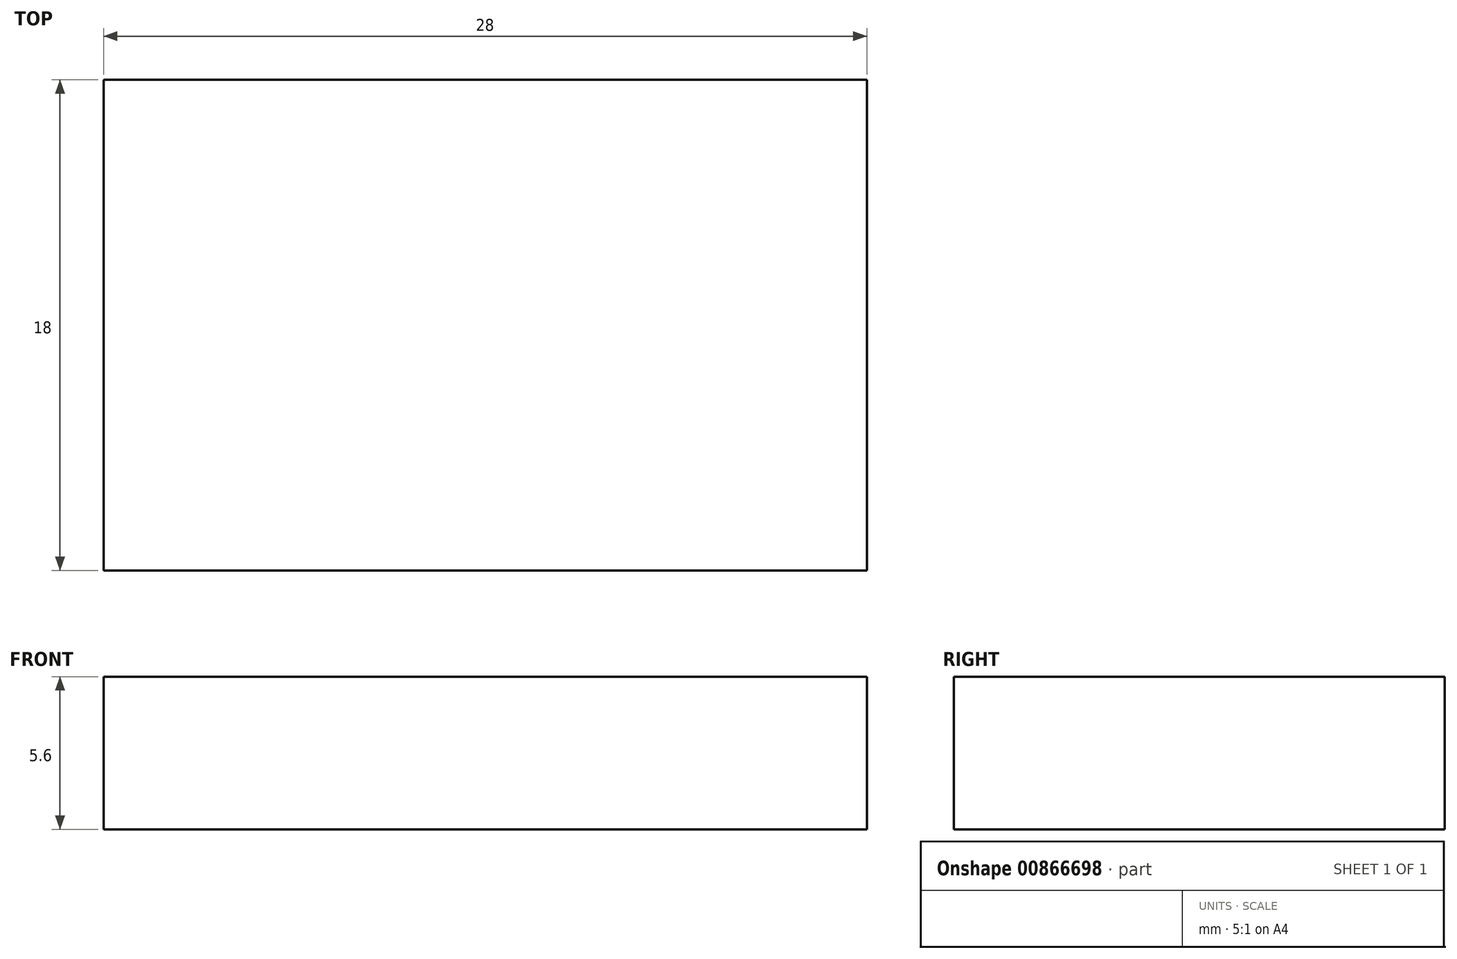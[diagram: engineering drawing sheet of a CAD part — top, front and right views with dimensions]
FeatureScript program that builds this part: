
annotation { "Feature Type Name" : "Feature", "Feature Type Description" : "" }
export const myFeature = defineFeature(function(context is Context, id is Id, definition is map)
    precondition{}
    {
        {
            var Q0;
            Q0=qCreatedBy(makeId("Top.planeOp"),FACE);
            var sketch = newSketch(context, id + "F0", { "sketchPlane" : qUnion([Q0])});
            skLineSegment(sketch, "E0.bottom", {"start": v(14, -9) * mm, "end": v(-14, -9) * mm});
            skLineSegment(sketch, "E0.top", {"start": v(14, 9) * mm, "end": v(-14, 9) * mm});
            skLineSegment(sketch, "E0.left", {"start": v(14, -9) * mm, "end": v(14, 9) * mm});
            skLineSegment(sketch, "E0.right", {"start": v(-14, -9) * mm, "end": v(-14, 9) * mm});
            skPoint(sketch, "E0.middle", {"position": v(0, 0) * mm});
            skSolve(sketch);
        }
        {
            var Q0;
            Q0=makeQuery(id+"F0.imprint","IMPRINT",FACE,{"disambiguationData":[TD([[makeQuery(id+"F0.imprint","IMPRINT",EDGE,{"derivedFrom":sQuery(id+"F0.wireOp",EDGE,"E0.bottom")}),-1.0]])]});
            extrude(context, id + "F1", {"entities" : qUnion([Q0]), "depth" : 5.6 * mm, "offsetDistance" : 25 * mm});
        }
    });
